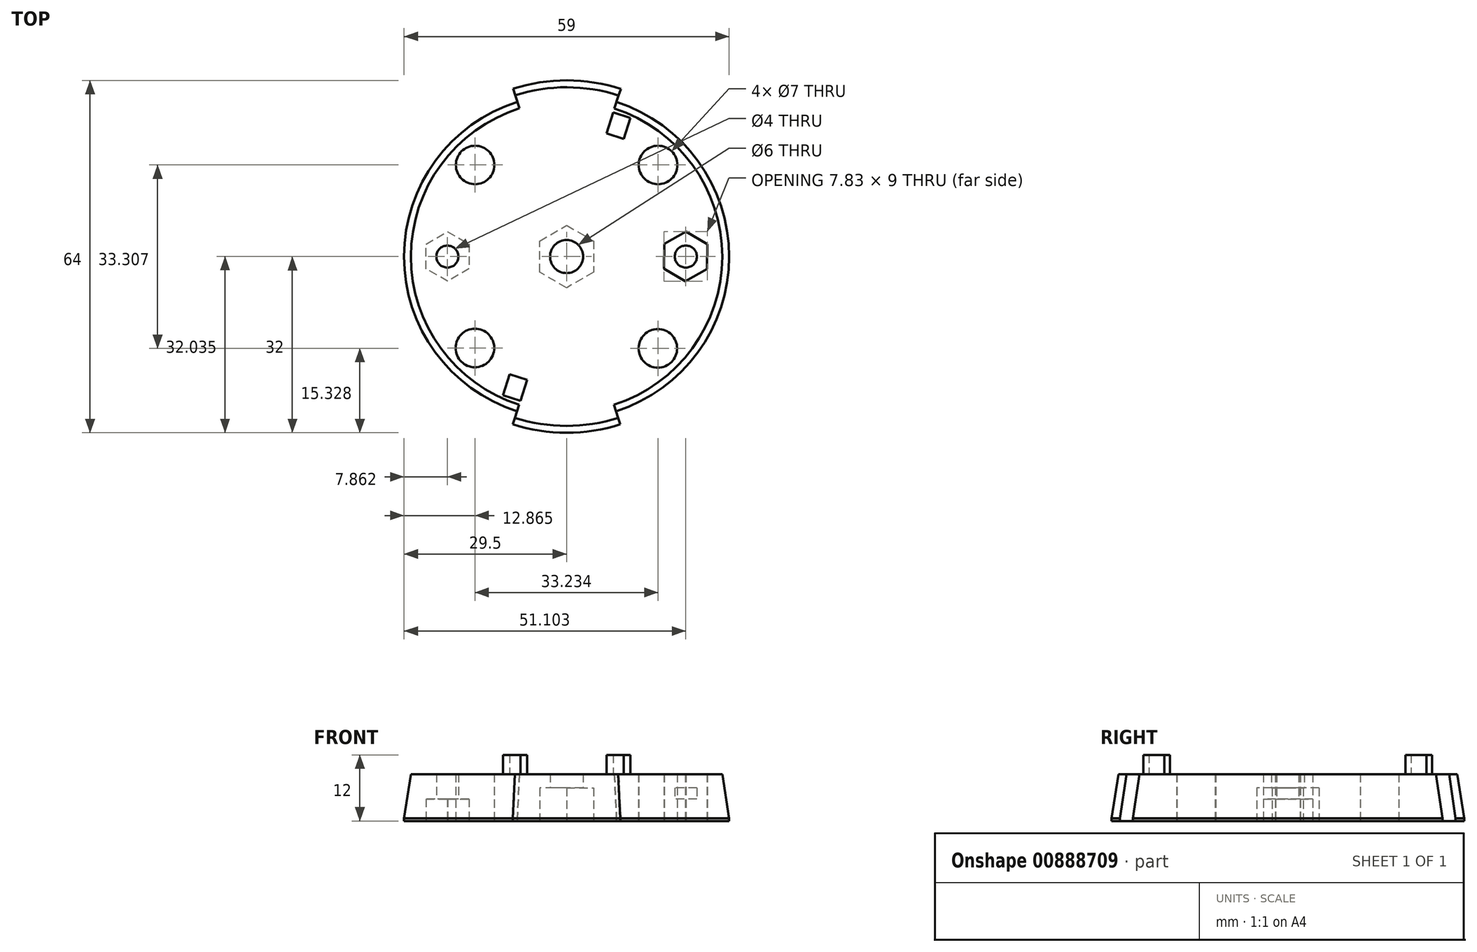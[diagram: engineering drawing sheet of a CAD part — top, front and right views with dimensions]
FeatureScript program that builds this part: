
annotation { "Feature Type Name" : "Feature", "Feature Type Description" : "" }
export const myFeature = defineFeature(function(context is Context, id is Id, definition is map)
    precondition{}
    {
        {
            var Q0;
            Q0=qCreatedBy(makeId("Top.planeOp"),FACE);
            var sketch = newSketch(context, id + "F0", { "sketchPlane" : qUnion([Q0])});
            skCircle(sketch, "E0", {"center": v(0, 0) * mm, "radius": 32 * mm});
            skCircle(sketch, "E1.cCircle", {"center": v(0, 0) * mm, "radius": 4.9 * mm, "construction": true});
            skLineSegment(sketch, "E1.0", {"start": v(4.9, 2.83) * mm, "end": v(4.9, -2.83) * mm});
            skLineSegment(sketch, "E1.1", {"start": v(4.9, -2.83) * mm, "end": v(0, -5.66) * mm});
            skLineSegment(sketch, "E1.2", {"start": v(0, -5.66) * mm, "end": v(-4.9, -2.83) * mm});
            skLineSegment(sketch, "E1.3", {"start": v(-4.9, -2.83) * mm, "end": v(-4.9, 2.83) * mm});
            skLineSegment(sketch, "E1.4", {"start": v(-4.9, 2.83) * mm, "end": v(0, 5.66) * mm});
            skLineSegment(sketch, "E1.5", {"start": v(0, 5.66) * mm, "end": v(4.9, 2.83) * mm});
            skPoint(sketch, "E1.0.midPoint", {"position": v(4.9, 0) * mm});
            skCircle(sketch, "E2", {"center": v(0, 0) * mm, "radius": 3.38 * mm});
            skCircle(sketch, "E3", {"center": v(0, 0) * mm, "radius": 29.5 * mm});
            skCircle(sketch, "E4", {"center": v(-29.5, 0) * mm, "radius": 4.3 * mm, "construction": true});
            skCircle(sketch, "E5.cCircle", {"center": v(-21.6, 0.03) * mm, "radius": 4.5 * mm, "construction": true});
            skLineSegment(sketch, "E5.0", {"start": v(-21.57, -4.47) * mm, "end": v(-25.48, -2.25) * mm});
            skLineSegment(sketch, "E5.1", {"start": v(-25.48, -2.25) * mm, "end": v(-25.52, 2.25) * mm});
            skLineSegment(sketch, "E5.2", {"start": v(-25.52, 2.25) * mm, "end": v(-21.64, 4.53) * mm});
            skLineSegment(sketch, "E5.3", {"start": v(-21.64, 4.53) * mm, "end": v(-17.72, 2.31) * mm});
            skLineSegment(sketch, "E5.4", {"start": v(-17.72, 2.31) * mm, "end": v(-17.69, -2.19) * mm});
            skLineSegment(sketch, "E5.5", {"start": v(-17.69, -2.19) * mm, "end": v(-21.57, -4.47) * mm});
            skLineSegment(sketch, "E6", {"start": v(0, 5.66) * mm, "end": v(0, -5.66) * mm, "construction": true});
            skLineSegment(sketch, "E7", {"start": v(0, 0) * mm, "end": v(-35.07, 35.15) * mm, "construction": true});
            skLineSegment(sketch, "E8", {"start": v(0, 0) * mm, "end": v(-62.76, 0.07) * mm, "construction": true});
            skLineSegment(sketch, "E9", {"start": v(0, -32) * mm, "end": v(0, -45.25) * mm, "construction": true});
            skLineSegment(sketch, "E10", {"start": v(0, -45.25) * mm, "end": v(-9, -45.25) * mm, "construction": true});
            skLineSegment(sketch, "E11", {"start": v(-9, -45.25) * mm, "end": v(-9, -28.1) * mm, "construction": true});
            skLineSegment(sketch, "E12", {"start": v(-9, -28.1) * mm, "end": v(9, -28.1) * mm, "construction": true});
            skLineSegment(sketch, "E13", {"start": v(0, 0) * mm, "end": v(-9.76, -30.47) * mm, "construction": true});
            skLineSegment(sketch, "E14", {"start": v(-9, -28.1) * mm, "end": v(-9.76, -30.47) * mm});
            skLineSegment(sketch, "E15.MirrorCS", {"start": v(0, 0) * mm, "end": v(9.76, -30.47) * mm, "construction": true});
            skLineSegment(sketch, "E16", {"start": v(9, -28.1) * mm, "end": v(9.76, -30.47) * mm});
            skLineSegment(sketch, "E17.MirrorCS", {"start": v(-8.94, 28.11) * mm, "end": v(-9.7, 30.5) * mm});
            skLineSegment(sketch, "E18.MirrorCS", {"start": v(0, 0) * mm, "end": v(9.83, 30.45) * mm, "construction": true});
            skLineSegment(sketch, "E19.MirrorCS", {"start": v(9.06, 28.07) * mm, "end": v(9.83, 30.45) * mm});
            skCircle(sketch, "E20", {"center": v(-29.5, 0) * mm, "radius": 4 * mm, "construction": true});
            skLineSegment(sketch, "E21.MirrorCS", {"start": v(25.52, 2.25) * mm, "end": v(21.64, 4.53) * mm});
            skLineSegment(sketch, "E22.MirrorCS", {"start": v(25.48, -2.25) * mm, "end": v(25.52, 2.25) * mm});
            skLineSegment(sketch, "E23.MirrorCS", {"start": v(21.57, -4.47) * mm, "end": v(25.48, -2.25) * mm});
            skLineSegment(sketch, "E24.MirrorCS", {"start": v(17.69, -2.19) * mm, "end": v(21.57, -4.47) * mm});
            skLineSegment(sketch, "E25.MirrorCS", {"start": v(17.72, 2.31) * mm, "end": v(17.69, -2.19) * mm});
            skLineSegment(sketch, "E26.MirrorCS", {"start": v(21.64, 4.53) * mm, "end": v(17.72, 2.31) * mm});
            skCircle(sketch, "E27", {"center": v(-20.84, 20.88) * mm, "radius": 2.5 * mm, "construction": true});
            skLineSegment(sketch, "E28", {"start": v(-19.07, 19.11) * mm, "end": v(-16.6, 16.64) * mm, "construction": true});
            skCircle(sketch, "E29", {"center": v(-16.6, 16.64) * mm, "radius": 3.5 * mm});
            skCircle(sketch, "E30.MirrorC", {"center": v(16.6, 16.64) * mm, "radius": 3.5 * mm});
            skCircle(sketch, "E31.MirrorC", {"center": v(-16.64, -16.6) * mm, "radius": 3.5 * mm});
            skCircle(sketch, "E32.MirrorC", {"center": v(16.56, -16.67) * mm, "radius": 3.5 * mm});
            skSolve(sketch);
        }
        {
            var Q0;
            Q0=makeQuery(id+"F0.imprint","IMPRINT",FACE,{"disambiguationData":[TD([[makeQuery(id+"F0.imprint","IMPRINT",EDGE,{"derivedFrom":sQuery(id+"F0.wireOp",EDGE,"E1.0")}),1.0]])]});
            var Q1;
            {var subQ0=sQuery(id+"F0.wireOp",EDGE,"E17.MirrorCS");Q1=makeQuery(id+"F0.imprint","IMPRINT",FACE,{"disambiguationData":[TD([[makeQuery(id+"F0.imprint","IMPRINT",EDGE,{"derivedFrom":subQ0}),-1.0]])]});}
            var Q2;
            {var subQ0=sQuery(id+"F0.wireOp",EDGE,"E14");Q2=makeQuery(id+"F0.imprint","IMPRINT",FACE,{"disambiguationData":[TD([[makeQuery(id+"F0.imprint","IMPRINT",EDGE,{"derivedFrom":subQ0}),1.0]])]});}
            extrude(context, id + "F1", {"entities" : qUnion([Q0, Q1, Q2]), "depth" : 4 * mm, "offsetDistance" : 25 * mm});
        }
        {
            var Q0;
            Q0=makeQuery(id+"F1.opExtrude","CAP_FACE",FACE,{"disambiguationData":[OSD([sQuery(id+"F0.wireOp",EDGE,"E0"),sQuery(id+"F0.wireOp",EDGE,"E1.0"),sQuery(id+"F0.wireOp",EDGE,"E1.1"),sQuery(id+"F0.wireOp",EDGE,"E1.2"),sQuery(id+"F0.wireOp",EDGE,"E1.3"),sQuery(id+"F0.wireOp",EDGE,"E1.4"),sQuery(id+"F0.wireOp",EDGE,"E1.5"),sQuery(id+"F0.wireOp",EDGE,"E3"),sQuery(id+"F0.wireOp",EDGE,"E5.0"),sQuery(id+"F0.wireOp",EDGE,"E5.1"),sQuery(id+"F0.wireOp",EDGE,"E5.2"),sQuery(id+"F0.wireOp",EDGE,"E5.3"),sQuery(id+"F0.wireOp",EDGE,"E5.4"),sQuery(id+"F0.wireOp",EDGE,"E5.5"),sQuery(id+"F0.wireOp",EDGE,"E14"),sQuery(id+"F0.wireOp",EDGE,"E16"),sQuery(id+"F0.wireOp",EDGE,"E17.MirrorCS"),sQuery(id+"F0.wireOp",EDGE,"E19.MirrorCS"),sQuery(id+"F0.wireOp",EDGE,"E21.MirrorCS"),sQuery(id+"F0.wireOp",EDGE,"E22.MirrorCS"),sQuery(id+"F0.wireOp",EDGE,"E23.MirrorCS"),sQuery(id+"F0.wireOp",EDGE,"E24.MirrorCS"),sQuery(id+"F0.wireOp",EDGE,"E25.MirrorCS"),sQuery(id+"F0.wireOp",EDGE,"E26.MirrorCS"),sQuery(id+"F0.wireOp",EDGE,"E29"),sQuery(id+"F0.wireOp",EDGE,"E30.MirrorC"),sQuery(id+"F0.wireOp",EDGE,"E31.MirrorC"),sQuery(id+"F0.wireOp",EDGE,"E32.MirrorC")])],"isStart":false});
            var sketch = newSketch(context, id + "F2", { "sketchPlane" : qUnion([Q0])});
            skCircle(sketch, "E33", {"center": v(-21.64, 0) * mm, "radius": 2 * mm});
            skLineSegment(sketch, "E34", {"start": v(0, 0) * mm, "end": v(0, 7.5) * mm, "construction": true});
            skCircle(sketch, "E35.MirrorC", {"center": v(21.64, 0) * mm, "radius": 2 * mm});
            skSolve(sketch);
        }
        {
            var Q0;
            Q0=makeQuery(id+"F2.imprint","IMPRINT",FACE,{"disambiguationData":[TD([[makeQuery(id+"F2.imprint","IMPRINT",EDGE,{"derivedFrom":makeQuery(id+"F1.opExtrude","CAP_EDGE",EDGE,{"disambiguationData":[OSD([sQuery(id+"F0.wireOp",EDGE,"E1.0")])],"isStart":false})}),1.0]])]});
            var Q1;
            Q1=makeQuery(id+"F2.imprint","IMPRINT",FACE,{"disambiguationData":[TD([[makeQuery(id+"F2.imprint","IMPRINT",EDGE,{"derivedFrom":sQuery(id+"F2.wireOp",EDGE,"E33")}),-1.0]])]});
            var Q2;
            Q2=makeQuery(id+"F2.imprint","IMPRINT",FACE,{"disambiguationData":[TD([[makeQuery(id+"F2.imprint","IMPRINT",EDGE,{"derivedFrom":sQuery(id+"F2.wireOp",EDGE,"E35.MirrorC")}),1.0]])]});
            extrude(context, id + "F3", {"entities" : qUnion([Q0, Q1, Q2]), "operationType" : NewBodyOperationType.ADD, "depth" : 2 * mm, "offsetDistance" : 25 * mm});
        }
        {
            var Q0;
            Q0=makeQuery(id+"F3.opExtrude","CAP_FACE",FACE,{"disambiguationData":[OSD([sQuery(id+"F0.wireOp",EDGE,"E0"),sQuery(id+"F0.wireOp",EDGE,"E1.0"),sQuery(id+"F0.wireOp",EDGE,"E1.1"),sQuery(id+"F0.wireOp",EDGE,"E1.2"),sQuery(id+"F0.wireOp",EDGE,"E1.3"),sQuery(id+"F0.wireOp",EDGE,"E1.4"),sQuery(id+"F0.wireOp",EDGE,"E1.5"),sQuery(id+"F0.wireOp",EDGE,"E3"),sQuery(id+"F0.wireOp",EDGE,"E14"),sQuery(id+"F0.wireOp",EDGE,"E16"),sQuery(id+"F0.wireOp",EDGE,"E17.MirrorCS"),sQuery(id+"F0.wireOp",EDGE,"E19.MirrorCS"),sQuery(id+"F0.wireOp",EDGE,"E29"),sQuery(id+"F0.wireOp",EDGE,"E30.MirrorC"),sQuery(id+"F0.wireOp",EDGE,"E31.MirrorC"),sQuery(id+"F0.wireOp",EDGE,"E32.MirrorC"),sQuery(id+"F2.wireOp",EDGE,"E33"),sQuery(id+"F2.wireOp",EDGE,"E35.MirrorC")])],"isStart":false});
            var sketch = newSketch(context, id + "F4", { "sketchPlane" : qUnion([Q0])});
            skCircle(sketch, "E36", {"center": v(0, 0) * mm, "radius": 3 * mm});
            skSolve(sketch);
        }
        {
            var Q0;
            Q0=makeQuery(id+"F4.imprint","IMPRINT",FACE,{"disambiguationData":[TD([[makeQuery(id+"F4.imprint","IMPRINT",EDGE,{"derivedFrom":makeQuery(id+"F3.opExtrude","CAP_EDGE",EDGE,{"disambiguationData":[OSD([sQuery(id+"F2.wireOp",EDGE,"E33")])],"isStart":false})}),-1.0]])]});
            var Q1;
            Q1=makeQuery(id+"F4.imprint","IMPRINT",FACE,{"disambiguationData":[TD([[makeQuery(id+"F4.imprint","IMPRINT",EDGE,{"derivedFrom":sQuery(id+"F4.wireOp",EDGE,"E36")}),-1.0]])]});
            extrude(context, id + "F5", {"entities" : qUnion([Q0, Q1]), "operationType" : NewBodyOperationType.ADD, "depth" : 2.5 * mm, "offsetDistance" : 25 * mm});
        }
        {
            var Q0;
            Q0=makeQuery(id+"F5.opExtrude","CAP_FACE",FACE,{"disambiguationData":[OSD([sQuery(id+"F0.wireOp",EDGE,"E0"),sQuery(id+"F0.wireOp",EDGE,"E3"),sQuery(id+"F0.wireOp",EDGE,"E14"),sQuery(id+"F0.wireOp",EDGE,"E16"),sQuery(id+"F0.wireOp",EDGE,"E17.MirrorCS"),sQuery(id+"F0.wireOp",EDGE,"E19.MirrorCS"),sQuery(id+"F0.wireOp",EDGE,"E29"),sQuery(id+"F0.wireOp",EDGE,"E30.MirrorC"),sQuery(id+"F0.wireOp",EDGE,"E31.MirrorC"),sQuery(id+"F0.wireOp",EDGE,"E32.MirrorC"),sQuery(id+"F2.wireOp",EDGE,"E33"),sQuery(id+"F2.wireOp",EDGE,"E35.MirrorC"),sQuery(id+"F4.wireOp",EDGE,"E36")])],"isStart":false});
            var sketch = newSketch(context, id + "F6", { "sketchPlane" : qUnion([Q0])});
            skLineSegment(sketch, "E37", {"start": v(9.06, 28.07) * mm, "end": v(-9, -28.1) * mm, "construction": true});
            skCircle(sketch, "E38", {"center": v(-9, -28.1) * mm, "radius": 2 * mm, "construction": true});
            skLineSegment(sketch, "E39.bottom", {"start": v(-8.39, -26.19) * mm, "end": v(-11.53, -25.19) * mm});
            skLineSegment(sketch, "E39.top", {"start": v(-7.17, -22.38) * mm, "end": v(-10.32, -21.38) * mm});
            skLineSegment(sketch, "E39.left", {"start": v(-8.39, -26.19) * mm, "end": v(-7.17, -22.38) * mm});
            skLineSegment(sketch, "E39.right", {"start": v(-11.53, -25.19) * mm, "end": v(-10.32, -21.38) * mm});
            skLineSegment(sketch, "E40", {"start": v(0, 0) * mm, "end": v(12.53, -4.03) * mm, "construction": true});
            skLineSegment(sketch, "E41.MirrorCS", {"start": v(7.24, 22.36) * mm, "end": v(10.38, 21.36) * mm});
            skLineSegment(sketch, "E42.MirrorCS", {"start": v(11.6, 25.17) * mm, "end": v(10.38, 21.36) * mm});
            skLineSegment(sketch, "E43.MirrorCS", {"start": v(8.45, 26.17) * mm, "end": v(11.6, 25.17) * mm});
            skLineSegment(sketch, "E44", {"start": v(8.45, 26.17) * mm, "end": v(7.24, 22.36) * mm});
            skSolve(sketch);
        }
        {
            var Q0;
            Q0=makeQuery(id+"F6.imprint","IMPRINT",FACE,{"disambiguationData":[TD([[makeQuery(id+"F6.imprint","IMPRINT",EDGE,{"derivedFrom":sQuery(id+"F6.wireOp",EDGE,"E41.MirrorCS")}),1.0]])]});
            var Q1;
            Q1=makeQuery(id+"F6.imprint","IMPRINT",FACE,{"disambiguationData":[TD([[makeQuery(id+"F6.imprint","IMPRINT",EDGE,{"derivedFrom":sQuery(id+"F6.wireOp",EDGE,"E39.bottom")}),-1.0]])]});
            extrude(context, id + "F7", {"entities" : qUnion([Q0, Q1]), "operationType" : NewBodyOperationType.ADD, "depth" : 3.5 * mm, "offsetDistance" : 25 * mm});
        }
        {
            var Q0;
            {var subQ0=sQuery(id+"F0.wireOp",EDGE,"E3");Q0=makeQuery(id+"F5.opExtrude","CAP_EDGE",EDGE,{"disambiguationData":[OSD([subQ0]),TDD([makeQuery(id+"F4.imprint","IMPRINT",EDGE,{"derivedFrom":makeQuery(id+"F3.opExtrude","CAP_EDGE",EDGE,{"disambiguationData":[OSD([subQ0]),TDD([makeQuery(id+"F2.imprint","IMPRINT",EDGE,{"derivedFrom":makeQuery(id+"F1.opExtrude","CAP_EDGE",EDGE,{"disambiguationData":[OSD([subQ0]),TDD([makeQuery(id+"F0.imprint","IMPRINT",EDGE,{"disambiguationData":[TD([[makeQuery(id+"F0.imprint","INTERSECT",VERTEX,{"derivedFrom":[subQ0,sQuery(id+"F0.wireOp",EDGE,"E16")]}),-1.0]])],"derivedFrom":subQ0})])],"isStart":false})})])],"isStart":false})})])],"isStart":false});}
            var Q1;
            {var subQ0=sQuery(id+"F0.wireOp",EDGE,"E3");Q1=makeQuery(id+"F5.opExtrude","CAP_EDGE",EDGE,{"disambiguationData":[OSD([subQ0]),TDD([makeQuery(id+"F4.imprint","IMPRINT",EDGE,{"derivedFrom":makeQuery(id+"F3.opExtrude","CAP_EDGE",EDGE,{"disambiguationData":[OSD([subQ0]),TDD([makeQuery(id+"F2.imprint","IMPRINT",EDGE,{"derivedFrom":makeQuery(id+"F1.opExtrude","CAP_EDGE",EDGE,{"disambiguationData":[OSD([subQ0]),TDD([makeQuery(id+"F0.imprint","IMPRINT",EDGE,{"disambiguationData":[TD([[makeQuery(id+"F0.imprint","INTERSECT",VERTEX,{"derivedFrom":[subQ0,sQuery(id+"F0.wireOp",EDGE,"E14")]}),1.0]])],"derivedFrom":subQ0})])],"isStart":false})})])],"isStart":false})})])],"isStart":false});}
            var Q2;
            {var subQ0=sQuery(id+"F0.wireOp",EDGE,"E0");Q2=makeQuery(id+"F5.opExtrude","CAP_EDGE",EDGE,{"disambiguationData":[OSD([subQ0]),TDD([makeQuery(id+"F4.imprint","IMPRINT",EDGE,{"derivedFrom":makeQuery(id+"F3.opExtrude","CAP_EDGE",EDGE,{"disambiguationData":[OSD([subQ0]),TDD([makeQuery(id+"F2.imprint","IMPRINT",EDGE,{"derivedFrom":makeQuery(id+"F1.opExtrude","CAP_EDGE",EDGE,{"disambiguationData":[OSD([subQ0]),TDD([makeQuery(id+"F0.imprint","IMPRINT",EDGE,{"disambiguationData":[TD([[makeQuery(id+"F0.imprint","INTERSECT",VERTEX,{"derivedFrom":[subQ0,sQuery(id+"F0.wireOp",EDGE,"E14")]}),-1.0]])],"derivedFrom":subQ0})])],"isStart":false})})])],"isStart":false})})])],"isStart":false});}
            var Q3;
            {var subQ0=sQuery(id+"F0.wireOp",EDGE,"E0");Q3=makeQuery(id+"F5.opExtrude","CAP_EDGE",EDGE,{"disambiguationData":[OSD([subQ0]),TDD([makeQuery(id+"F4.imprint","IMPRINT",EDGE,{"derivedFrom":makeQuery(id+"F3.opExtrude","CAP_EDGE",EDGE,{"disambiguationData":[OSD([subQ0]),TDD([makeQuery(id+"F2.imprint","IMPRINT",EDGE,{"derivedFrom":makeQuery(id+"F1.opExtrude","CAP_EDGE",EDGE,{"disambiguationData":[OSD([subQ0]),TDD([makeQuery(id+"F0.imprint","IMPRINT",EDGE,{"disambiguationData":[TD([[makeQuery(id+"F0.imprint","INTERSECT",VERTEX,{"derivedFrom":[subQ0,sQuery(id+"F0.wireOp",EDGE,"E17.MirrorCS")]}),1.0]])],"derivedFrom":subQ0})])],"isStart":false})})])],"isStart":false})})])],"isStart":false});}
            chamfer(context, id + "F8", {"entities" : qUnion([Q0, Q1, Q2, Q3]), "chamferType" : ChamferType.TWO_OFFSETS, "width1" : 1.25 * mm, "oppositeDirection" : false, "width2" : 8 * mm, "tangentPropagation" : true});
        }
    });
